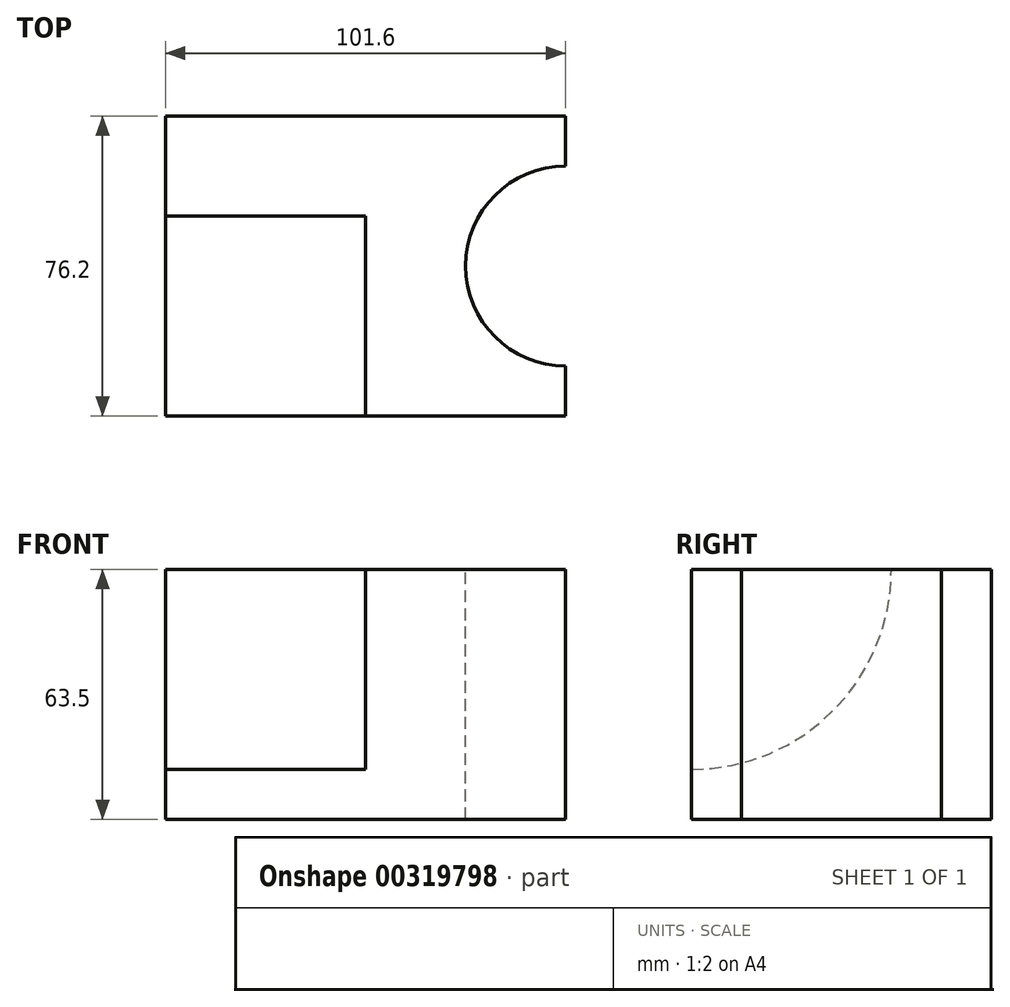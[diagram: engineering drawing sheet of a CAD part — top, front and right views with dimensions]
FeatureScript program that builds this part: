
annotation { "Feature Type Name" : "Feature", "Feature Type Description" : "" }
export const myFeature = defineFeature(function(context is Context, id is Id, definition is map)
    precondition{}
    {
        {
            var Q0;
            Q0=qCreatedBy(makeId("Front.planeOp"),FACE);
            var sketch = newSketch(context, id + "F0", { "sketchPlane" : qUnion([Q0])});
            skLineSegment(sketch, "E0.bottom", {"start": v(-37.77, 21.24) * mm, "end": v(63.83, 21.24) * mm});
            skLineSegment(sketch, "E0.top", {"start": v(-37.77, -42.26) * mm, "end": v(63.83, -42.26) * mm});
            skLineSegment(sketch, "E0.left", {"start": v(-37.77, 21.24) * mm, "end": v(-37.77, -42.26) * mm});
            skLineSegment(sketch, "E0.right", {"start": v(63.83, 21.24) * mm, "end": v(63.83, -42.26) * mm});
            skSolve(sketch);
        }
        {
            var Q0;
            Q0=makeQuery(id+"F0.imprint","IMPRINT",FACE,{"disambiguationData":[TD([[makeQuery(id+"F0.imprint","IMPRINT",EDGE,{"derivedFrom":sQuery(id+"F0.wireOp",EDGE,"E0.bottom")}),-1.0]])]});
            extrude(context, id + "F1", {"entities" : qUnion([Q0]), "oppositeDirection" : true, "depth" : 76.2 * mm});
        }
        {
            var Q0;
            Q0=makeQuery(id+"F1.opExtrude","SWEPT_FACE",FACE,{"disambiguationData":[OSD([sQuery(id+"F0.wireOp",EDGE,"E0.bottom")])]});
            var sketch = newSketch(context, id + "F2", { "sketchPlane" : qUnion([Q0])});
            skLineSegment(sketch, "E1", {"start": v(63.83, 76.2) * mm, "end": v(63.83, 0) * mm});
            skArc(sketch, "E2", {"start": v(63.83, 63.5) * mm, "mid": v(38.43, 38.1) * mm, "end": v(63.83, 12.7) * mm});
            skSolve(sketch);
        }
        {
            var Q0;
            {var subQ0=sQuery(id+"F2.wireOp",EDGE,"E2");Q0=makeQuery(id+"F2.imprint","IMPRINT",FACE,{"disambiguationData":[TD([[makeQuery(id+"F2.imprint","IMPRINT",EDGE,{"derivedFrom":subQ0}),1.0]])]});}
            extrude(context, id + "F3", {"entities" : qUnion([Q0]), "operationType" : NewBodyOperationType.REMOVE, "endBound" : BoundingType.THROUGH_ALL, "oppositeDirection" : true, "depth" : 25.4 * mm});
        }
        {
            var Q0;
            Q0=makeQuery(id+"F1.opExtrude","SWEPT_FACE",FACE,{"disambiguationData":[OSD([sQuery(id+"F0.wireOp",EDGE,"E0.left")])]});
            var sketch = newSketch(context, id + "F4", { "sketchPlane" : qUnion([Q0])});
            skArc(sketch, "E3", {"start": v(-50.8, 21.24) * mm, "mid": v(-35.92, -14.68) * mm, "end": v(0, -29.56) * mm});
            skLineSegment(sketch, "E4", {"start": v(0, 21.24) * mm, "end": v(-50.8, 21.24) * mm});
            skLineSegment(sketch, "E5", {"start": v(0, 21.24) * mm, "end": v(0, -29.56) * mm});
            skSolve(sketch);
        }
        {
            var Q0;
            Q0=makeQuery(id+"F4.imprint","IMPRINT",FACE,{"disambiguationData":[TD([[makeQuery(id+"F4.imprint","IMPRINT",EDGE,{"derivedFrom":sQuery(id+"F4.wireOp",EDGE,"E3")}),1.0]])]});
            extrude(context, id + "F5", {"entities" : qUnion([Q0]), "operationType" : NewBodyOperationType.REMOVE, "oppositeDirection" : true, "depth" : 50.8 * mm});
        }
    });
